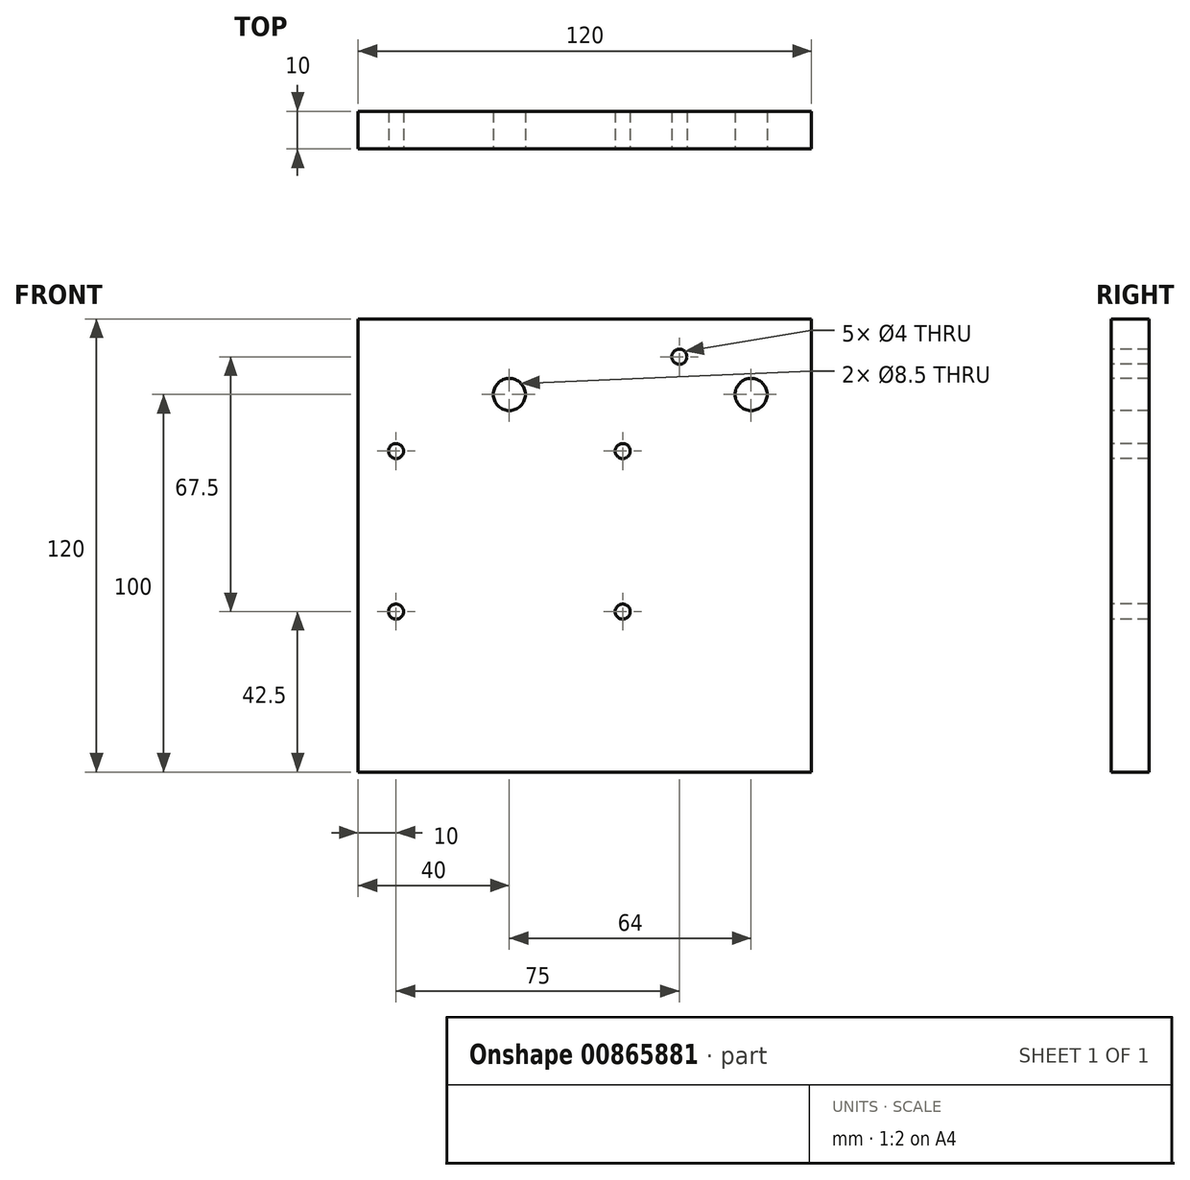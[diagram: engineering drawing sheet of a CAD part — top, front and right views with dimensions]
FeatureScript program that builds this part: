
annotation { "Feature Type Name" : "Feature", "Feature Type Description" : "" }
export const myFeature = defineFeature(function(context is Context, id is Id, definition is map)
    precondition{}
    {
        {
            var Q0;
            Q0=qCreatedBy(makeId("Front.planeOp"),FACE);
            var sketch = newSketch(context, id + "F0", { "sketchPlane" : qUnion([Q0])});
            skLineSegment(sketch, "E0.bottom", {"start": v(0, 0) * mm, "end": v(120, 0) * mm});
            skLineSegment(sketch, "E0.top", {"start": v(0, 120) * mm, "end": v(120, 120) * mm});
            skLineSegment(sketch, "E0.left", {"start": v(0, 0) * mm, "end": v(0, 120) * mm});
            skLineSegment(sketch, "E0.right", {"start": v(120, 0) * mm, "end": v(120, 120) * mm});
            skSolve(sketch);
        }
        {
            var Q0;
            Q0 = qSketchRegion(id + "F0", true);
            extrude(context, id + "F1", {"entities" : qUnion([Q0]), "depth" : 10 * mm, "offsetDistance" : 25 * mm});
        }
        {
            var Q0;
            Q0=makeQuery(id+"F1.opExtrude","CAP_FACE",FACE,{"disambiguationData":[OSD([sQuery(id+"F0.wireOp",EDGE,"E0.bottom"),sQuery(id+"F0.wireOp",EDGE,"E0.top"),sQuery(id+"F0.wireOp",EDGE,"E0.left"),sQuery(id+"F0.wireOp",EDGE,"E0.right")])],"isStart":false});
            var sketch = newSketch(context, id + "F2", { "sketchPlane" : qUnion([Q0])});
            skCircle(sketch, "E1", {"center": v(40, 100) * mm, "radius": 4.25 * mm});
            skCircle(sketch, "E2", {"center": v(104, 100) * mm, "radius": 4.25 * mm});
            skCircle(sketch, "E3", {"center": v(85, 110) * mm, "radius": 2 * mm});
            skSolve(sketch);
        }
        {
            var Q0;
            Q0 = qSketchRegion(id + "F2", true);
            extrude(context, id + "F3", {"entities" : qUnion([Q0]), "operationType" : NewBodyOperationType.REMOVE, "endBound" : BoundingType.THROUGH_ALL, "oppositeDirection" : true, "depth" : 25 * mm, "offsetDistance" : 25 * mm});
        }
        {
            var Q0;
            Q0=makeQuery(id+"F1.opExtrude","CAP_FACE",FACE,{"disambiguationData":[OSD([sQuery(id+"F0.wireOp",EDGE,"E0.bottom"),sQuery(id+"F0.wireOp",EDGE,"E0.top"),sQuery(id+"F0.wireOp",EDGE,"E0.left"),sQuery(id+"F0.wireOp",EDGE,"E0.right")])],"isStart":false});
            var sketch = newSketch(context, id + "F4", { "sketchPlane" : qUnion([Q0])});
            skCircle(sketch, "E4", {"center": v(10, 42.5) * mm, "radius": 2 * mm});
            skCircle(sketch, "E5", {"center": v(10, 85) * mm, "radius": 2 * mm});
            skCircle(sketch, "E6", {"center": v(70, 85) * mm, "radius": 2 * mm});
            skCircle(sketch, "E7", {"center": v(70, 42.5) * mm, "radius": 2 * mm});
            skSolve(sketch);
        }
        {
            var Q0;
            Q0 = qSketchRegion(id + "F4", true);
            extrude(context, id + "F5", {"entities" : qUnion([Q0]), "operationType" : NewBodyOperationType.REMOVE, "endBound" : BoundingType.THROUGH_ALL, "oppositeDirection" : true, "depth" : 25 * mm, "offsetDistance" : 25 * mm});
        }
    });
